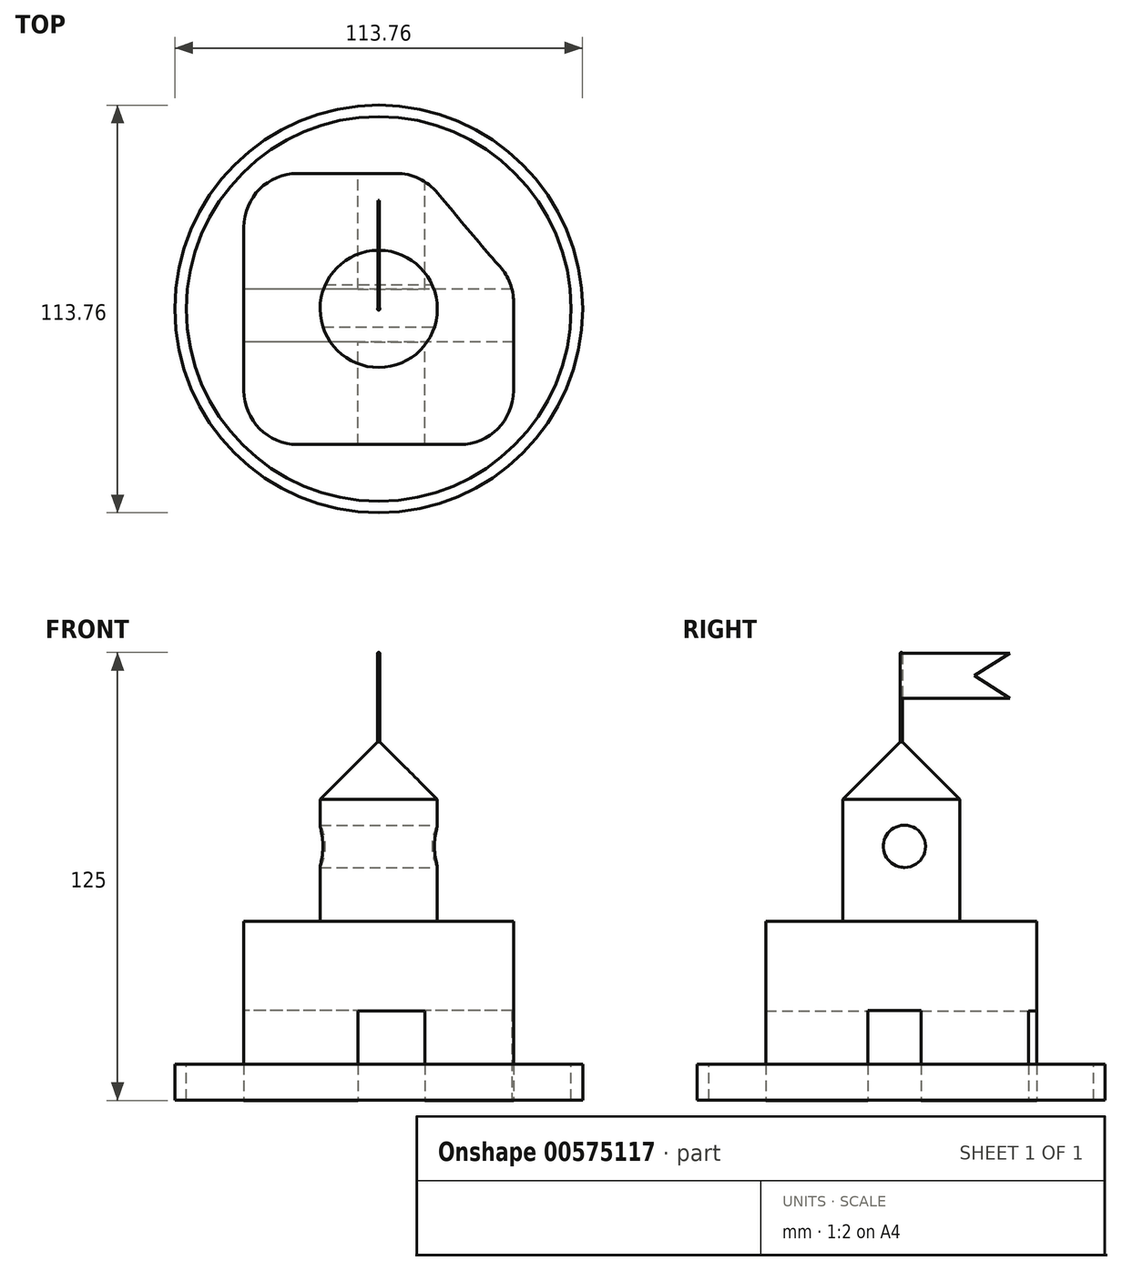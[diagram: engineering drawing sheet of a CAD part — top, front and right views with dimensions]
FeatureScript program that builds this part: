
annotation { "Feature Type Name" : "Feature", "Feature Type Description" : "" }
export const myFeature = defineFeature(function(context is Context, id is Id, definition is map)
    precondition{}
    {
        {
            var Q0;
            Q0=qCreatedBy(makeId("Top.planeOp"),FACE);
            var sketch = newSketch(context, id + "F0", { "sketchPlane" : qUnion([Q0])});
            skLineSegment(sketch, "E0.bottom", {"start": v(0, 0) * mm, "end": v(-75.22, 0) * mm});
            skLineSegment(sketch, "E0.top", {"start": v(0, -75.65) * mm, "end": v(-75.22, -75.65) * mm});
            skLineSegment(sketch, "E0.left", {"start": v(0, 0) * mm, "end": v(0, -75.65) * mm});
            skLineSegment(sketch, "E0.right", {"start": v(-75.22, 0) * mm, "end": v(-75.22, -75.65) * mm});
            skSolve(sketch);
        }
        {
            var Q0;
            Q0=makeQuery(id+"F0.imprint","IMPRINT",FACE,{"disambiguationData":[TD([[makeQuery(id+"F0.imprint","IMPRINT",EDGE,{"derivedFrom":sQuery(id+"F0.wireOp",EDGE,"E0.bottom")}),1.0]])]});
            extrude(context, id + "F1", {"entities" : qUnion([Q0]), "depth" : 50 * mm, "offsetDistance" : 25 * mm});
        }
        {
            var Q0;
            Q0=qCreatedBy(makeId("Top.planeOp"),FACE);
            var sketch = newSketch(context, id + "F2", { "sketchPlane" : qUnion([Q0])});
            skLineSegment(sketch, "E1.bottom", {"start": v(-24.79, -99.1) * mm, "end": v(-24.79, 11.7) * mm});
            skLineSegment(sketch, "E1.top", {"start": v(-43.44, -99.1) * mm, "end": v(-43.44, 11.7) * mm});
            skLineSegment(sketch, "E1.left", {"start": v(-24.79, -99.1) * mm, "end": v(-43.44, -99.1) * mm});
            skLineSegment(sketch, "E1.right", {"start": v(-24.79, 11.7) * mm, "end": v(-43.44, 11.7) * mm});
            skSolve(sketch);
        }
        {
            var Q0;
            Q0=makeQuery(id+"F2.imprint","IMPRINT",FACE,{"disambiguationData":[TD([[makeQuery(id+"F2.imprint","IMPRINT",EDGE,{"derivedFrom":sQuery(id+"F2.wireOp",EDGE,"E1.bottom")}),1.0]])]});
            extrude(context, id + "F3", {"entities" : qUnion([Q0]), "operationType" : NewBodyOperationType.REMOVE, "depth" : 25 * mm, "offsetDistance" : 25 * mm});
        }
        {
            var Q0;
            Q0=qCreatedBy(makeId("Top.planeOp"),FACE);
            var sketch = newSketch(context, id + "F4", { "sketchPlane" : qUnion([Q0])});
            skFitSpline(sketch, "E2", {"points": [v(0, 0) * mm, v(0.72, -29.8) * mm, v(0, -30) * mm, v(-25.6, 0) * mm, v(-25.6, 0.01) * mm, v(-25.3, 0.1) * mm, v(-0.23, 0.2) * mm, v(-0.02, 0.18) * mm, v(0, 0) * mm]});
            skSolve(sketch);
        }
        {
            var Q0;
            Q0 = qSketchRegion(id + "F4", true);
            extrude(context, id + "F5", {"entities" : qUnion([Q0]), "operationType" : NewBodyOperationType.REMOVE, "oppositeDirection" : true, "depth" : -60 * mm, "offsetDistance" : 25 * mm});
        }
        {
            var Q0;
            Q0=makeQuery(id+"F5.boolean.opBoolean","INTERSECT",EDGE,{"derivedFrom":[makeQuery(id+"F1.opExtrude","SWEPT_FACE",FACE,{"disambiguationData":[OSD([sQuery(id+"F0.wireOp",EDGE,"E0.left")])]}),makeQuery(id+"F5.opExtrude","SWEPT_FACE",FACE,{"disambiguationData":[OSD([sQuery(id+"F4.wireOp",EDGE,"E2")])]})]});
            var Q1;
            Q1=makeQuery(id+"F1.opExtrude","SWEPT_EDGE",EDGE,{"disambiguationData":[OSD([sQuery(id+"F0.wireOp",EDGE,"E0.top"),sQuery(id+"F0.wireOp",EDGE,"E0.left")])]});
            var Q2;
            Q2=makeQuery(id+"F1.opExtrude","SWEPT_EDGE",EDGE,{"disambiguationData":[OSD([sQuery(id+"F0.wireOp",EDGE,"E0.top"),sQuery(id+"F0.wireOp",EDGE,"E0.right")])]});
            var Q3;
            Q3=makeQuery(id+"F1.opExtrude","SWEPT_EDGE",EDGE,{"disambiguationData":[OSD([sQuery(id+"F0.wireOp",EDGE,"E0.bottom"),sQuery(id+"F0.wireOp",EDGE,"E0.right")])]});
            var Q4;
            Q4=makeQuery(id+"F5.boolean.opBoolean","INTERSECT",EDGE,{"derivedFrom":[makeQuery(id+"F1.opExtrude","SWEPT_FACE",FACE,{"disambiguationData":[OSD([sQuery(id+"F0.wireOp",EDGE,"E0.bottom")])]}),makeQuery(id+"F5.opExtrude","SWEPT_FACE",FACE,{"disambiguationData":[OSD([sQuery(id+"F4.wireOp",EDGE,"E2")])]})]});
            fillet(context, id + "F6", {"entities" : qUnion([Q0, Q1, Q2, Q3, Q4]), "radius" : 15 * mm, "tangentPropagation" : true, "allowEdgeOverflow" : false});
        }
        {
            var Q0;
            Q0=makeQuery(id+"F1.opExtrude","CAP_FACE",FACE,{"disambiguationData":[OSD([sQuery(id+"F0.wireOp",EDGE,"E0.bottom"),sQuery(id+"F0.wireOp",EDGE,"E0.top"),sQuery(id+"F0.wireOp",EDGE,"E0.left"),sQuery(id+"F0.wireOp",EDGE,"E0.right")])],"isStart":false});
            var sketch = newSketch(context, id + "F7", { "sketchPlane" : qUnion([Q0])});
            skCircle(sketch, "E3", {"center": v(-37.6, -37.83) * mm, "radius": 16.35 * mm});
            skLineSegment(sketch, "E4", {"start": v(-37.6, -75.65) * mm, "end": v(-37.6, 0) * mm});
            skSolve(sketch);
        }
        {
            var Q0;
            Q0 = qSketchRegion(id + "F7", true);
            extrude(context, id + "F8", {"entities" : qUnion([Q0]), "depth" : 50 * mm, "offsetDistance" : 25 * mm});
        }
        {
            var Q0;
            Q0=makeQuery(id+"F8.opExtrude","CAP_EDGE",EDGE,{"disambiguationData":[OSD([sQuery(id+"F7.wireOp",EDGE,"E3")])],"isStart":false});
            chamfer(context, id + "F9", {"entities" : qUnion([Q0]), "width" : 16 * mm, "tangentPropagation" : true});
        }
        {
            var Q0;
            Q0=qCreatedBy(makeId("Right.planeOp"),FACE);
            var sketch = newSketch(context, id + "F10", { "sketchPlane" : qUnion([Q0])});
            skCircle(sketch, "E5", {"center": v(-36.92, 70.91) * mm, "radius": 5.89 * mm});
            skSolve(sketch);
        }
        {
            var Q0;
            Q0 = qSketchRegion(id + "F10", true);
            extrude(context, id + "F11", {"entities" : qUnion([Q0]), "operationType" : NewBodyOperationType.REMOVE, "endBound" : BoundingType.THROUGH_ALL, "oppositeDirection" : true, "depth" : 25 * mm, "offsetDistance" : 25 * mm});
        }
        {
            var Q0;
            Q0=makeQuery(id+"F1.opExtrude","SWEPT_FACE",FACE,{"disambiguationData":[OSD([sQuery(id+"F0.wireOp",EDGE,"E0.right")])]});
            var sketch = newSketch(context, id + "F12", { "sketchPlane" : qUnion([Q0])});
            skLineSegment(sketch, "E6.bottom", {"start": v(32.33, 0) * mm, "end": v(47.1, 0) * mm});
            skLineSegment(sketch, "E6.top", {"start": v(32.33, 25.06) * mm, "end": v(47.1, 25.06) * mm});
            skLineSegment(sketch, "E6.left", {"start": v(32.33, 0) * mm, "end": v(32.33, 25.06) * mm});
            skLineSegment(sketch, "E6.right", {"start": v(47.1, 0) * mm, "end": v(47.1, 25.06) * mm});
            skSolve(sketch);
        }
        {
            var Q0;
            Q0=makeQuery(id+"F12.imprint","IMPRINT",FACE,{"disambiguationData":[TD([[makeQuery(id+"F12.imprint","IMPRINT",EDGE,{"derivedFrom":sQuery(id+"F12.wireOp",EDGE,"E6.bottom")}),1.0]])]});
            extrude(context, id + "F13", {"entities" : qUnion([Q0]), "operationType" : NewBodyOperationType.REMOVE, "endBound" : BoundingType.THROUGH_ALL, "oppositeDirection" : true, "depth" : 25 * mm, "offsetDistance" : 25 * mm});
        }
        {
            var Q0;
            Q0=makeQuery(id+"F8.opExtrude","CAP_FACE",FACE,{"disambiguationData":[OSD([sQuery(id+"F7.wireOp",EDGE,"E3")])],"isStart":false});
            var sketch = newSketch(context, id + "F14", { "sketchPlane" : qUnion([Q0])});
            skCircle(sketch, "E7", {"center": v(-37.6, -37.83) * mm, "radius": 0.3 * mm});
            skSolve(sketch);
        }
        {
            var Q0;
            Q0 = qSketchRegion(id + "F14", true);
            extrude(context, id + "F15", {"entities" : qUnion([Q0]), "operationType" : NewBodyOperationType.ADD, "depth" : 25 * mm, "offsetDistance" : 25 * mm});
        }
        {
            var Q0;
            Q0=makeQuery(id+"F15.opExtrude","CAP_FACE",FACE,{"disambiguationData":[OSD([sQuery(id+"F14.wireOp",EDGE,"E7")])],"isStart":false});
            fillet(context, id + "F16", {"entities" : qUnion([Q0]), "radius" : .2 * mm, "tangentPropagation" : true, "allowEdgeOverflow" : false});
        }
        {
            var Q0;
            Q0 = qSketchRegion(id + "F10", true);
            extrude(context, id + "F17", {"entities" : qUnion([Q0]), "operationType" : NewBodyOperationType.REMOVE, "endBound" : BoundingType.THROUGH_ALL, "oppositeDirection" : true, "depth" : 25 * mm, "offsetDistance" : 25 * mm});
        }
        {
            var Q0;
            Q0=makeQuery(id+"F1.opExtrude","CAP_FACE",FACE,{"disambiguationData":[OSD([sQuery(id+"F0.wireOp",EDGE,"E0.bottom"),sQuery(id+"F0.wireOp",EDGE,"E0.top"),sQuery(id+"F0.wireOp",EDGE,"E0.left"),sQuery(id+"F0.wireOp",EDGE,"E0.right")])],"isStart":false});
            var sketch = newSketch(context, id + "F18", { "sketchPlane" : qUnion([Q0])});
            skLineSegment(sketch, "E8", {"start": v(-75.22, -37.83) * mm, "end": v(0, -37.83) * mm});
            skSolve(sketch);
        }
        {
            var Q0;
            Q0=sQuery(id+"F18.wireOp",EDGE,"E8");
            cPlane(context, id + "F19", {"entities" : qUnion([Q0]), "cplaneType" : CPlaneType.MID_PLANE, "offset" : 25 * mm, "width" : 150 * mm, "height" : 150 * mm});
        }
        {
            var Q0;
            Q0=qCreatedBy(id+"F19.planeOp",FACE);
            var sketch = newSketch(context, id + "F20", { "sketchPlane" : qUnion([Q0])});
            skLineSegment(sketch, "E9.bottom", {"start": v(-37.72, 124.8) * mm, "end": v(-7.5, 124.8) * mm});
            skLineSegment(sketch, "E9.top", {"start": v(-37.72, 112.21) * mm, "end": v(-7.5, 112.21) * mm});
            skLineSegment(sketch, "E9.left", {"start": v(-37.72, 124.8) * mm, "end": v(-37.72, 112.21) * mm});
            skLineSegment(sketch, "E10", {"start": v(-7.5, 118.5) * mm, "end": v(-37.72, 118.5) * mm, "construction": true});
            skLineSegment(sketch, "E11", {"start": v(-7.5, 124.8) * mm, "end": v(-17.42, 118.5) * mm});
            skLineSegment(sketch, "E12", {"start": v(-17.42, 118.5) * mm, "end": v(-7.5, 112.21) * mm});
            skSolve(sketch);
        }
        {
            var Q0;
            Q0=makeQuery(id+"F20.imprint","IMPRINT",FACE,{"disambiguationData":[TD([[makeQuery(id+"F20.imprint","IMPRINT",EDGE,{"derivedFrom":sQuery(id+"F20.wireOp",EDGE,"E9.bottom")}),-1.0]])]});
            extrude(context, id + "F21", {"entities" : qUnion([Q0]), "depth" : .15 * mm, "offsetDistance" : 25 * mm, "hasSecondDirection" : true, "secondDirectionOppositeDirection" : true, "secondDirectionDepth" : .15 * mm});
        }
        {
            var Q0;
            Q0=qCreatedBy(makeId("Front.planeOp"),FACE);
            var sketch = newSketch(context, id + "F22", { "sketchPlane" : qUnion([Q0])});
            skLineSegment(sketch, "E13.bottom", {"start": v(0.45, 0.13) * mm, "end": v(4.87, 0.13) * mm});
            skLineSegment(sketch, "E13.top", {"start": v(0.45, 10.16) * mm, "end": v(4.87, 10.16) * mm});
            skLineSegment(sketch, "E13.left", {"start": v(0.45, 0.13) * mm, "end": v(0.45, 10.16) * mm});
            skLineSegment(sketch, "E13.right", {"start": v(4.87, 0.13) * mm, "end": v(4.87, 10.16) * mm});
            skSolve(sketch);
        }
        {
            var Q0;
            Q0=makeQuery(id+"F22.imprint","IMPRINT",FACE,{"disambiguationData":[TD([[makeQuery(id+"F22.imprint","IMPRINT",EDGE,{"derivedFrom":sQuery(id+"F22.wireOp",EDGE,"E13.bottom")}),1.0]])]});
            var Q1;
            Q1=makeQuery(id+"F8.opExtrude","SWEPT_FACE",FACE,{"disambiguationData":[OSD([sQuery(id+"F7.wireOp",EDGE,"E3")])]});
            revolve(context, id + "F23", {"entities" : qUnion([Q0]), "axis" : qUnion([Q1]), "revolveType" : RevolveType.TWO_DIRECTIONS, "angle" : 340 * degree, "angleBack" : 340 * degree});
        }
    });
